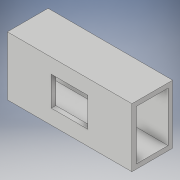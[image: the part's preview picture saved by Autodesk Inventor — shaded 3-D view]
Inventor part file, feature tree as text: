
AUTODESK INVENTOR PART (.ipt)
format: ipt  version: 2018 (Build 220112000, 112)  size: 104,960 bytes
history: native  units: in
note: dims shown in document units (in); Inventor stores cm internally (conversion verified against a paired STEP export)
features: extrude x2, sketch x2, shell x1
ambient origin geometry x8: Origin, YZ Plane, XZ Plane, XY Plane, X Axis, Y Axis, Z Axis, Center Point
bodies: Solid1 (feature_tree)
feature tree (5):
  extrude  "Extrusion1"  Depth=1.3in
  shell  "Shell1"  Thickness=0.9in
  extrude  "Extrusion2"  Depth=0.1in TaperAngle=0.0deg
  sketch  "Sketch1"  dims[d0=2.75in d1=1.3in d2=0.9in d3=0.0in]
  sketch  "Sketch2"  dims[d4=0.1in d9=0.1in d10=0.0in]
